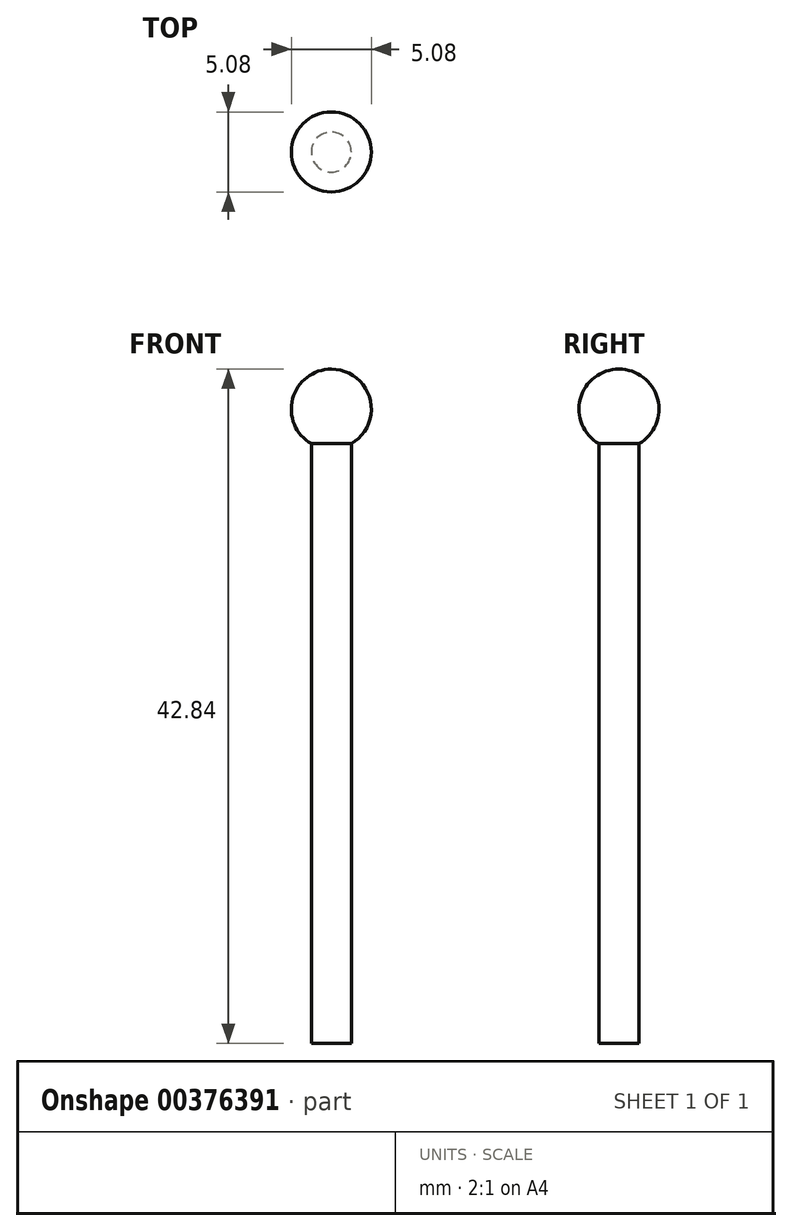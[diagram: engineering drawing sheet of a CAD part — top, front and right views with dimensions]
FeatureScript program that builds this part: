
annotation { "Feature Type Name" : "Feature", "Feature Type Description" : "" }
export const myFeature = defineFeature(function(context is Context, id is Id, definition is map)
    precondition{}
    {
        {
            var Q0;
            Q0=qCreatedBy(makeId("Front.planeOp"),FACE);
            var sketch = newSketch(context, id + "F0", { "sketchPlane" : qUnion([Q0])});
            skLineSegment(sketch, "E0", {"start": v(1.27, 0) * mm, "end": v(1.27, 38.1) * mm});
            skLineSegment(sketch, "E1", {"start": v(0, 42.84) * mm, "end": v(0, 0) * mm});
            skLineSegment(sketch, "E2", {"start": v(0, 0) * mm, "end": v(1.27, 0) * mm});
            skArc(sketch, "E3", {"start": v(1.27, 38.1) * mm, "mid": v(2.45, 40.96) * mm, "end": v(0, 42.84) * mm});
            skSolve(sketch);
        }
        {
            var Q0;
            Q0=makeQuery(id+"F0.imprint","IMPRINT",FACE,{"disambiguationData":[TD([[makeQuery(id+"F0.imprint","IMPRINT",EDGE,{"derivedFrom":sQuery(id+"F0.wireOp",EDGE,"E0")}),1.0]])]});
            var Q1;
            Q1=sQuery(id+"F0.wireOp",EDGE,"E1");
            revolve(context, id + "F1", {"entities" : qUnion([Q0]), "axis" : qUnion([Q1]), "revolveType" : RevolveType.FULL});
        }
    });
